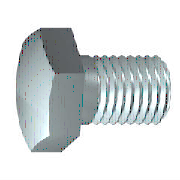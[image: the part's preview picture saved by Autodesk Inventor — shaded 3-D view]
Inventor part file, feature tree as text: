
AUTODESK INVENTOR PART (.ipt)
format: ipt  version: 2015 (Build 190159000, 159)  size: 188,416 bytes
history: native  units: mm (DEFAULTED — no unit token found)
features: other x4, plane x3, sketch x2
ambient origin geometry x6: Origin, XY Plane, X Axis, Y Axis, Z Axis, Center Point
bodies: Body1 (feature_tree)
feature tree (9):
  plane  "WorkPlane1"
  other  "WorkPoint1"
  other  "MSC_A1"
  other  "MSC_PF1"
  other  "MSC_PT1"
  plane  "WorkPlane2"
  plane  "WorkPlane3"
  sketch  "Szkic3"
  sketch  "Szkic4"
